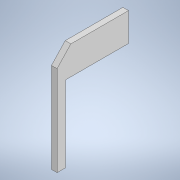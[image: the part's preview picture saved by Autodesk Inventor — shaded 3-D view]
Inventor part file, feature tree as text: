
AUTODESK INVENTOR PART (.ipt)
format: ipt  version: 2020 (Build 240168000, 168)  size: 129,536 bytes
history: native  units: in
note: dims shown in document units (in); Inventor stores cm internally (conversion verified against a paired STEP export)
features: extrude x2, sketch x2
ambient origin geometry x8: Origin, YZ Plane, XZ Plane, XY Plane, X Axis, Y Axis, Z Axis, Center Point
bodies: Solid1 (feature_tree)
feature tree (4):
  extrude  "Extrusion1"  Depth=0.375in
  extrude  "Extrusion3"  Depth=0.25in TaperAngle=0.0deg
  sketch  "Sketch1"  dims[d0=1.0in d1=0.375in]
  sketch  "Sketch4"  dims[d3=0.8in d4=0.25in d5=0.0in d11=2.0in d12=0.25in d13=3.0in d14=0.375in d15=0.64in d16=0.0in]
